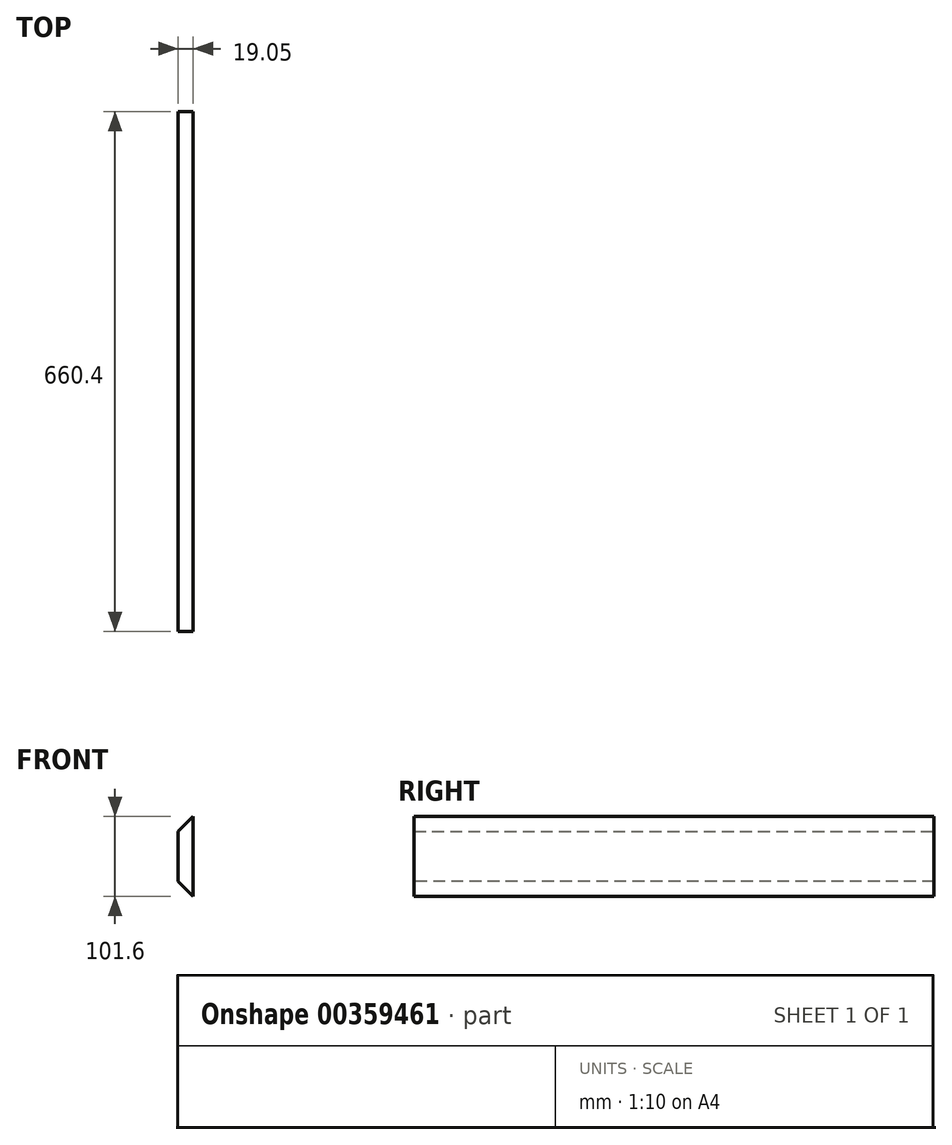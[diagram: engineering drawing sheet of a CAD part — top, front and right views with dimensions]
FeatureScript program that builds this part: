
annotation { "Feature Type Name" : "Feature", "Feature Type Description" : "" }
export const myFeature = defineFeature(function(context is Context, id is Id, definition is map)
    precondition{}
    {
        {
            var Q0;
            Q0=qCreatedBy(makeId("Right.planeOp"),FACE);
            var sketch = newSketch(context, id + "F0", { "sketchPlane" : qUnion([Q0])});
            skLineSegment(sketch, "E0.bottom", {"start": v(0, 0) * mm, "end": v(660.4, 0) * mm});
            skLineSegment(sketch, "E0.top", {"start": v(0, 101.6) * mm, "end": v(660.4, 101.6) * mm});
            skLineSegment(sketch, "E0.left", {"start": v(0, 0) * mm, "end": v(0, 101.6) * mm});
            skLineSegment(sketch, "E0.right", {"start": v(660.4, 0) * mm, "end": v(660.4, 101.6) * mm});
            skSolve(sketch);
        }
        {
            var Q0;
            Q0=makeQuery(id+"F0.imprint","IMPRINT",FACE,{"disambiguationData":[TD([[makeQuery(id+"F0.imprint","IMPRINT",EDGE,{"derivedFrom":sQuery(id+"F0.wireOp",EDGE,"E0.bottom")}),1.0]])]});
            extrude(context, id + "F1", {"entities" : qUnion([Q0]), "depth" : 19.05 * mm});
        }
        {
            var Q0;
            Q0=makeQuery(id+"F1.opExtrude","CAP_EDGE",EDGE,{"disambiguationData":[OSD([sQuery(id+"F0.wireOp",EDGE,"E0.top")])],"isStart":true});
            var Q1;
            Q1=makeQuery(id+"F1.opExtrude","CAP_EDGE",EDGE,{"disambiguationData":[OSD([sQuery(id+"F0.wireOp",EDGE,"E0.bottom")])],"isStart":true});
            chamfer(context, id + "F2", {"entities" : qUnion([Q0, Q1]), "width" : 19.05 * mm, "tangentPropagation" : true});
        }
    });
